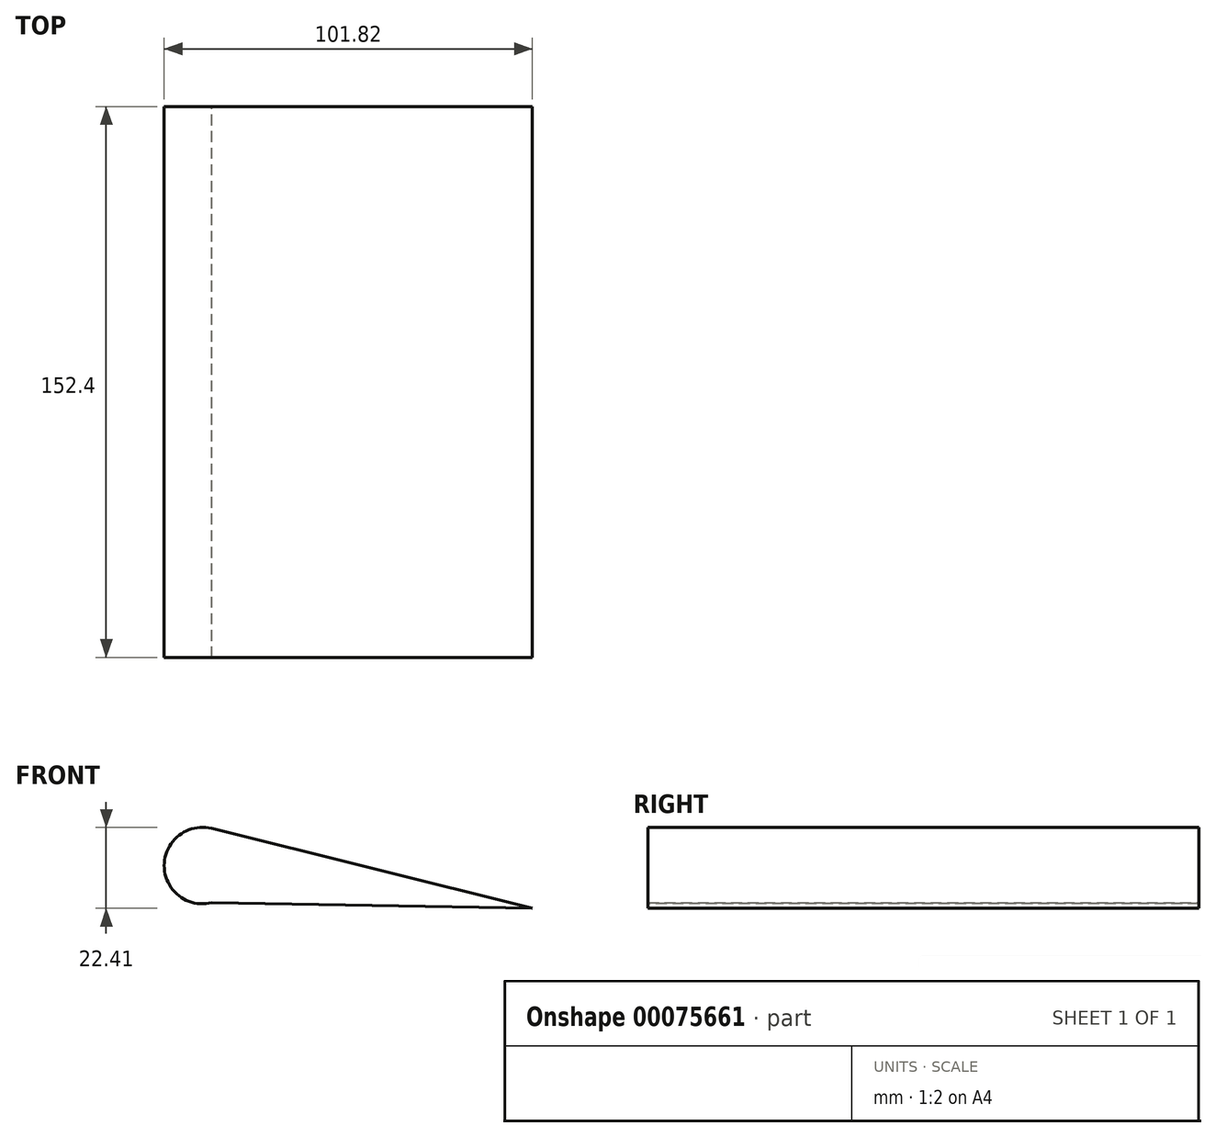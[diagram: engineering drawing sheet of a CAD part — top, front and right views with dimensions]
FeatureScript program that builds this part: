
annotation { "Feature Type Name" : "Feature", "Feature Type Description" : "" }
export const myFeature = defineFeature(function(context is Context, id is Id, definition is map)
    precondition{}
    {
        {
            var Q0;
            Q0=qCreatedBy(makeId("Front.planeOp"),FACE);
            var sketch = newSketch(context, id + "F0", { "sketchPlane" : qUnion([Q0])});
            skLineSegment(sketch, "E0", {"start": v(-46.55, 37.09) * mm, "end": v(42.14, 15) * mm});
            skLineSegment(sketch, "E1", {"start": v(42.14, 15) * mm, "end": v(-46.55, 16.57) * mm});
            skArc(sketch, "E2", {"start": v(-46.55, 37.09) * mm, "mid": v(-59.68, 26.83) * mm, "end": v(-46.55, 16.57) * mm});
            skSolve(sketch);
        }
        {
            var Q0;
            Q0=qCreatedBy(makeId("Front.planeOp"),FACE);
            cPlane(context, id + "F1", {"entities" : qUnion([Q0]), "cplaneType" : CPlaneType.OFFSET, "offset" : 152.4 * mm, "width" : 152.4 * mm, "height" : 152.4 * mm});
        }
        {
            var Q0;
            Q0=qCreatedBy(id+"F1.planeOp",FACE);
            var sketch = newSketch(context, id + "F2", { "sketchPlane" : qUnion([Q0])});
            skLineSegment(sketch, "E3.0", {"start": v(-46.55, 37.09) * mm, "end": v(42.14, 15) * mm});
            skLineSegment(sketch, "E4.0", {"start": v(42.14, 15) * mm, "end": v(-46.55, 16.57) * mm});
            skArc(sketch, "E5.0", {"start": v(-46.55, 37.09) * mm, "mid": v(-59.68, 26.83) * mm, "end": v(-46.55, 16.57) * mm});
            skSolve(sketch);
        }
        {
            var Q0;
            Q0=makeQuery(id+"F2.imprint","IMPRINT",FACE,{"disambiguationData":[TD([[makeQuery(id+"F2.imprint","IMPRINT",EDGE,{"derivedFrom":sQuery(id+"F2.wireOp",EDGE,"E3.0")}),-1.0]])]});
            var Q1;
            Q1=makeQuery(id+"F0.imprint","IMPRINT",FACE,{"disambiguationData":[TD([[makeQuery(id+"F0.imprint","IMPRINT",EDGE,{"derivedFrom":sQuery(id+"F0.wireOp",EDGE,"E0")}),-1.0]])]});
            loft(context, id + "F3", {"sheetProfilesArray" : [{ "sheetProfileEntities" : qUnion([Q0]) }, { "sheetProfileEntities" : qUnion([Q1]) }]});
        }
    });
